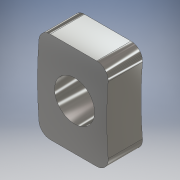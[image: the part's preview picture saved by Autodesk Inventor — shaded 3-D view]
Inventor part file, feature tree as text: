
AUTODESK INVENTOR PART (.ipt)
format: ipt  version: 2017 (Build 210142000, 142)  size: 140,288 bytes
history: native  units: mm
features: extrude x2, sketch x2, fillet x1, projected_geometry x1
ambient origin geometry x8: Origin, YZ Plane, XZ Plane, XY Plane, X Axis, Y Axis, Z Axis, Center Point
bodies: Solid1 (feature_tree)
feature tree (6):
  extrude  "Extrusion1"  Depth=40.5mm
  extrude  "Extrusion2"  Depth=1.0mm
  fillet  "Fillet1"  Radius=4.0mm
  sketch  "Sketch1"  dims[d7=0.0mm d8=40.5mm]
  sketch  "Sketch2"  dims[d9=35.5mm d14=4.0mm d15=4.0mm d18=4.0mm d19=4.0mm d20=3.0mm d21=0.0mm d22=3.5mm d23=0.0mm d24=0.0mm d25=1.0mm]
  projected_geometry  "Projected Loop1"
